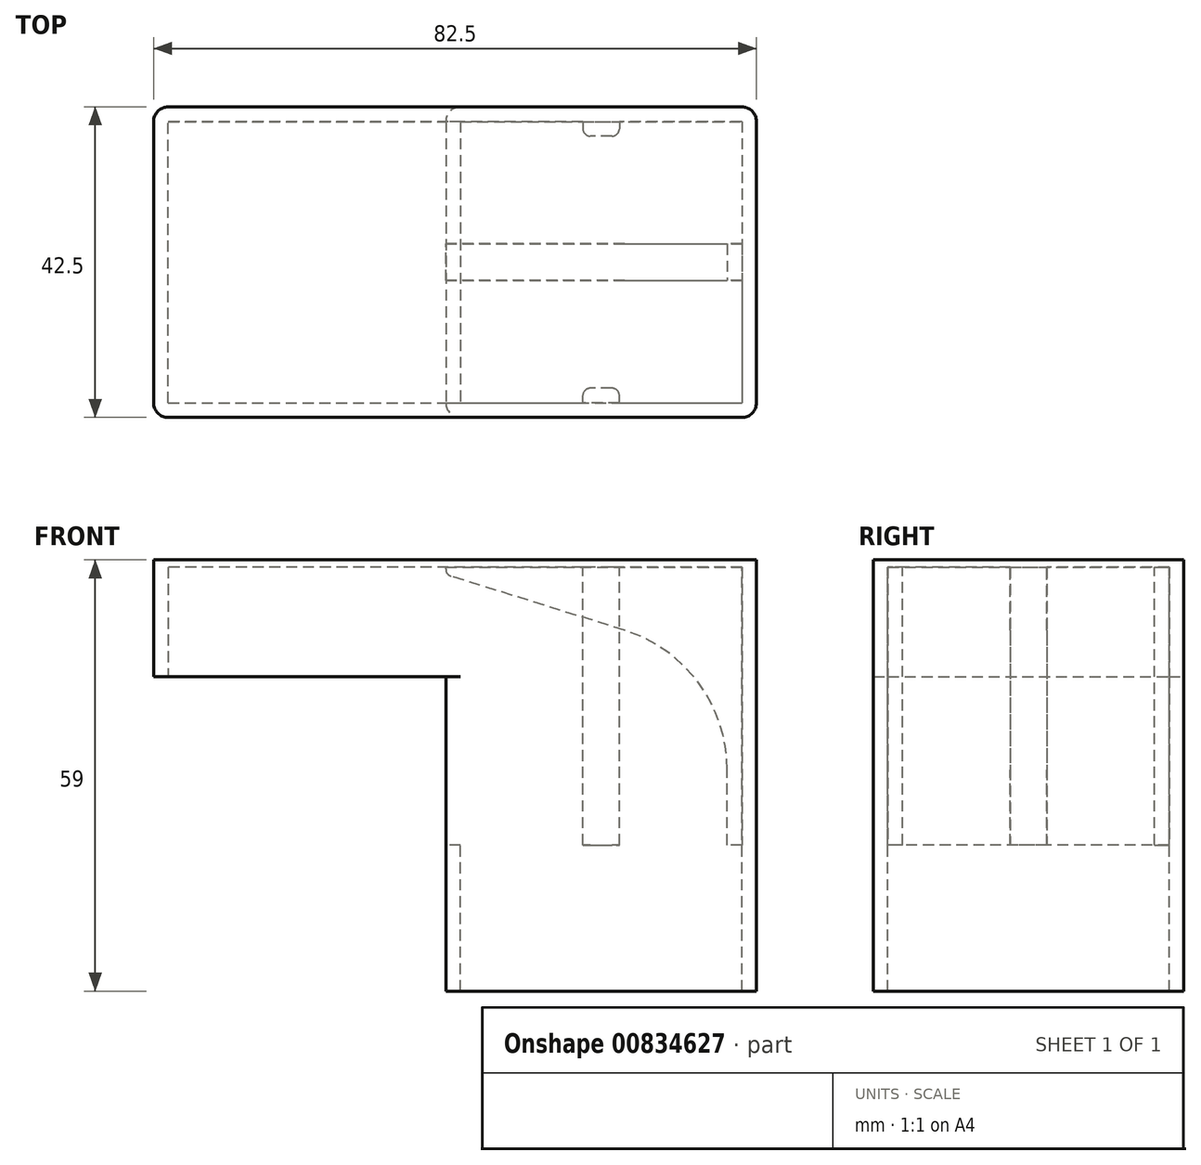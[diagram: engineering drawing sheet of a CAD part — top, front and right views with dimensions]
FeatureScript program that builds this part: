
annotation { "Feature Type Name" : "Feature", "Feature Type Description" : "" }
export const myFeature = defineFeature(function(context is Context, id is Id, definition is map)
    precondition{}
    {
        {
            var Q0;
            Q0=qCreatedBy(makeId("Top.planeOp"),FACE);
            var sketch = newSketch(context, id + "F0", { "sketchPlane" : qUnion([Q0])});
            skLineSegment(sketch, "E0.bottom", {"start": v(-19.25, 19.25) * mm, "end": v(19.25, 19.25) * mm});
            skLineSegment(sketch, "E0.top", {"start": v(-19.25, -19.25) * mm, "end": v(19.25, -19.25) * mm});
            skLineSegment(sketch, "E0.left", {"start": v(-19.25, 19.25) * mm, "end": v(-19.25, -19.25) * mm});
            skLineSegment(sketch, "E0.right", {"start": v(19.25, 19.25) * mm, "end": v(19.25, -19.25) * mm});
            skPoint(sketch, "E0.middle", {"position": v(0, 0) * mm});
            skLineSegment(sketch, "E1.0", {"start": v(-21.25, 21.25) * mm, "end": v(-21.25, -21.25) * mm});
            skLineSegment(sketch, "E1.1", {"start": v(-21.25, 21.25) * mm, "end": v(21.25, 21.25) * mm});
            skLineSegment(sketch, "E1.2", {"start": v(21.25, 21.25) * mm, "end": v(21.25, -21.25) * mm});
            skLineSegment(sketch, "E1.3", {"start": v(-21.25, -21.25) * mm, "end": v(21.25, -21.25) * mm});
            skSolve(sketch);
        }
        {
            var Q0;
            Q0=makeQuery(id+"F0.imprint","IMPRINT",FACE,{"disambiguationData":[TD([[makeQuery(id+"F0.imprint","IMPRINT",EDGE,{"derivedFrom":sQuery(id+"F0.wireOp",EDGE,"E0.bottom")}),1.0]])]});
            extrude(context, id + "F1", {"entities" : qUnion([Q0]), "oppositeDirection" : true, "depth" : 20 * mm, "offsetDistance" : 25 * mm});
        }
        {
            var Q0;
            Q0=makeQuery(id+"F0.imprint","IMPRINT",FACE,{"disambiguationData":[TD([[makeQuery(id+"F0.imprint","IMPRINT",EDGE,{"derivedFrom":sQuery(id+"F0.wireOp",EDGE,"E0.bottom")}),1.0]])]});
            var sketch = newSketch(context, id + "F2", { "sketchPlane" : qUnion([Q0])});
            skLineSegment(sketch, "E2.0", {"start": v(-21.25, -21.25) * mm, "end": v(21.25, -21.25) * mm});
            skLineSegment(sketch, "E3.0", {"start": v(21.25, 21.25) * mm, "end": v(21.25, -21.25) * mm});
            skLineSegment(sketch, "E4.0", {"start": v(19.25, 19.25) * mm, "end": v(19.25, -19.25) * mm});
            skLineSegment(sketch, "E5.0", {"start": v(-21.25, 21.25) * mm, "end": v(21.25, 21.25) * mm});
            skLineSegment(sketch, "E6.0", {"start": v(-21.25, 21.25) * mm, "end": v(-21.25, 19.25) * mm});
            skLineSegment(sketch, "E7", {"start": v(19.25, -19.25) * mm, "end": v(-21.25, -19.25) * mm});
            skLineSegment(sketch, "E8", {"start": v(19.25, 19.25) * mm, "end": v(-21.25, 19.25) * mm});
            skLineSegment(sketch, "E9.trimOffspring", {"start": v(-21.25, -19.25) * mm, "end": v(-21.25, -21.25) * mm});
            skSolve(sketch);
        }
        {
            var Q0;
            Q0=makeQuery(id+"F2.imprint","IMPRINT",FACE,{"disambiguationData":[TD([[makeQuery(id+"F2.imprint","IMPRINT",EDGE,{"derivedFrom":sQuery(id+"F2.wireOp",EDGE,"E2.0")}),1.0]])]});
            extrude(context, id + "F3", {"entities" : qUnion([Q0]), "operationType" : NewBodyOperationType.ADD, "depth" : 38 * mm, "offsetDistance" : 25 * mm});
        }
        {
            var Q0;
            Q0=makeQuery(id+"F3.opExtrude","CAP_FACE",FACE,{"disambiguationData":[OSD([sQuery(id+"F2.wireOp",EDGE,"E2.0"),sQuery(id+"F2.wireOp",EDGE,"E3.0"),sQuery(id+"F2.wireOp",EDGE,"E4.0"),sQuery(id+"F2.wireOp",EDGE,"E5.0"),sQuery(id+"F2.wireOp",EDGE,"E6.0"),sQuery(id+"F2.wireOp",EDGE,"E7"),sQuery(id+"F2.wireOp",EDGE,"E8"),sQuery(id+"F2.wireOp",EDGE,"E9.trimOffspring")])],"isStart":false});
            var sketch = newSketch(context, id + "F4", { "sketchPlane" : qUnion([Q0])});
            skLineSegment(sketch, "E10.bottom", {"start": v(-21.25, -21.25) * mm, "end": v(21.25, -21.25) * mm});
            skLineSegment(sketch, "E10.top", {"start": v(-21.25, 21.25) * mm, "end": v(21.25, 21.25) * mm});
            skLineSegment(sketch, "E10.left", {"start": v(-21.25, -21.25) * mm, "end": v(-21.25, 21.25) * mm});
            skLineSegment(sketch, "E10.right", {"start": v(21.25, -21.25) * mm, "end": v(21.25, 21.25) * mm});
            skSolve(sketch);
        }
        {
            var Q0;
            Q0 = qSketchRegion(id + "F4", true);
            extrude(context, id + "F5", {"entities" : qUnion([Q0]), "operationType" : NewBodyOperationType.ADD, "depth" : 1 * mm, "offsetDistance" : 25 * mm});
        }
        {
            var Q0;
            Q0=makeQuery(id+"F1.opExtrude","CAP_EDGE",EDGE,{"disambiguationData":[OSD([sQuery(id+"F0.wireOp",EDGE,"E0.left")])],"isStart":false});
            cPoint(context, id + "F6", {"entities" : qUnion([Q0]), "parameter" : 0.5});
        }
        {
            var Q0;
            Q0=makeQuery(id+"F3.boolean.opBoolean","MERGE",FACE,{"derivedFrom":[makeQuery(id+"F1.opExtrude","SWEPT_FACE",FACE,{"disambiguationData":[OSD([sQuery(id+"F0.wireOp",EDGE,"E0.top")])]}),makeQuery(id+"F3.opExtrude","SWEPT_FACE",FACE,{"disambiguationData":[OSD([sQuery(id+"F2.wireOp",EDGE,"E7")])]})]});
            var Q1;
            Q1 = qCreatedBy(id + "F6" ,VERTEX);
            cPlane(context, id + "F7", {"entities" : qUnion([Q0, Q1]), "cplaneType" : CPlaneType.PLANE_POINT, "offset" : 25 * mm, "width" : 150 * mm, "height" : 150 * mm});
        }
        {
            var Q0;
            Q0=qCreatedBy(id+"F7.planeOp",FACE);
            var sketch = newSketch(context, id + "F8", { "sketchPlane" : qUnion([Q0])});
            skLineSegment(sketch, "E11.0", {"start": v(21.25, 38) * mm, "end": v(21.25, 37.74) * mm, "construction": true});
            skLineSegment(sketch, "E12.0", {"start": v(21.25, 38) * mm, "end": v(-19.25, 38) * mm});
            skLineSegment(sketch, "E13", {"start": v(-19.25, 38) * mm, "end": v(-19.25, 0) * mm});
            skLineSegment(sketch, "E14", {"start": v(-19.25, 0) * mm, "end": v(-17.25, 0) * mm});
            skLineSegment(sketch, "E15", {"start": v(-17.25, 0) * mm, "end": v(-17.25, 10.28) * mm});
            skLineSegment(sketch, "E16", {"start": v(-3.2, 29.38) * mm, "end": v(20.55, 36.78) * mm});
            skLineSegment(sketch, "E17", {"start": v(21.25, 37) * mm, "end": v(21.25, 38) * mm});
            skPoint(sketch, "E18.visualSharp", {"position": v(-17.25, 0) * mm});
            skLineSegment(sketch, "E18.filletArc", {"start": v(-17.25, 0) * mm, "end": v(-17.25, 0) * mm});
            skPoint(sketch, "E19.visualSharp", {"position": v(-17.25, 25) * mm});
            skArc(sketch, "E19.filletArc", {"start": v(-3.2, 29.38) * mm, "mid": v(-13.36, 22.14) * mm, "end": v(-17.25, 10.28) * mm});
            skPoint(sketch, "E20.orphan", {"position": v(21.25, 0) * mm});
            skPoint(sketch, "E21.visualSharp", {"position": v(21.25, 37) * mm});
            skArc(sketch, "E21.filletArc", {"start": v(20.55, 36.78) * mm, "mid": v(21.06, 37.14) * mm, "end": v(21.25, 37.74) * mm});
            skSolve(sketch);
        }
        {
            var Q0;
            {var subQ0=sQuery(id+"F8.wireOp",EDGE,"E12.0");Q0=makeQuery(id+"F8.imprint","IMPRINT",FACE,{"disambiguationData":[TD([[makeQuery(id+"F8.imprint","IMPRINT",EDGE,{"derivedFrom":subQ0}),1.0]])]});}
            extrude(context, id + "F9", {"entities" : qUnion([Q0]), "operationType" : NewBodyOperationType.ADD, "endBound" : BoundingType.SYMMETRIC, "depth" : 5 * mm, "offsetDistance" : 25 * mm});
        }
        {
            var Q0;
            Q0=makeQuery(id+"F9.boolean.opBoolean","MERGE",FACE,{"derivedFrom":[makeQuery(id+"F5.boolean.opBoolean","MERGE",FACE,{"derivedFrom":[makeQuery(id+"F3.boolean.opBoolean","MERGE",FACE,{"derivedFrom":[makeQuery(id+"F1.opExtrude","SWEPT_FACE",FACE,{"disambiguationData":[OSD([sQuery(id+"F0.wireOp",EDGE,"E1.0")])]}),makeQuery(id+"F3.opExtrude","SWEPT_FACE",FACE,{"disambiguationData":[OSD([sQuery(id+"F2.wireOp",EDGE,"E6.0")])]}),makeQuery(id+"F3.opExtrude","SWEPT_FACE",FACE,{"disambiguationData":[OSD([sQuery(id+"F2.wireOp",EDGE,"E9.trimOffspring")])]})]}),makeQuery(id+"F5.opExtrude","SWEPT_FACE",FACE,{"disambiguationData":[OSD([sQuery(id+"F4.wireOp",EDGE,"E10.left")])]})]}),makeQuery(id+"F9.opExtrude","SWEPT_FACE",FACE,{"disambiguationData":[OSD([sQuery(id+"F8.wireOp",EDGE,"E17")])]})]});
            var sketch = newSketch(context, id + "F10", { "sketchPlane" : qUnion([Q0])});
            skLineSegment(sketch, "E22.0", {"start": v(19.25, 38) * mm, "end": v(19.25, 23) * mm});
            skLineSegment(sketch, "E23.0", {"start": v(-19.25, 38) * mm, "end": v(-19.25, 23) * mm});
            skLineSegment(sketch, "E24.0", {"start": v(-21.25, 39) * mm, "end": v(21.25, 39) * mm});
            skLineSegment(sketch, "E25", {"start": v(19.25, 38) * mm, "end": v(-19.25, 38) * mm});
            skLineSegment(sketch, "E26", {"start": v(21.25, 39) * mm, "end": v(21.25, 23) * mm});
            skLineSegment(sketch, "E27", {"start": v(-21.25, 39) * mm, "end": v(-21.25, 23) * mm});
            skLineSegment(sketch, "E28", {"start": v(21.25, 23) * mm, "end": v(-21.25, 23) * mm});
            skPoint(sketch, "E29.end.orphan", {"position": v(19.25, 0) * mm});
            skPoint(sketch, "E29.start.orphan", {"position": v(21.25, 0) * mm});
            skPoint(sketch, "E30.trimOffspring.start.orphan", {"position": v(-19.25, 0) * mm});
            skSolve(sketch);
        }
        {
            var Q0;
            {var subQ4=sQuery(id+"F10.wireOp",EDGE,"E22.0");Q0=makeQuery(id+"F10.imprint","IMPRINT",FACE,{"disambiguationData":[TD([[makeQuery(id+"F10.imprint","IMPRINT",EDGE,{"derivedFrom":subQ4}),1.0]])]});}
            extrude(context, id + "F11", {"entities" : qUnion([Q0]), "operationType" : NewBodyOperationType.ADD, "depth" : 38 * mm, "offsetDistance" : 25 * mm});
        }
        {
            var Q0;
            Q0=makeQuery(id+"F11.opExtrude","CAP_FACE",FACE,{"disambiguationData":[OSD([sQuery(id+"F10.wireOp",EDGE,"E22.0"),sQuery(id+"F10.wireOp",EDGE,"E23.0"),sQuery(id+"F10.wireOp",EDGE,"E24.0"),sQuery(id+"F10.wireOp",EDGE,"E25"),sQuery(id+"F10.wireOp",EDGE,"E26"),sQuery(id+"F10.wireOp",EDGE,"E27"),sQuery(id+"F10.wireOp",EDGE,"E28")])],"isStart":false});
            var sketch = newSketch(context, id + "F12", { "sketchPlane" : qUnion([Q0])});
            skLineSegment(sketch, "E31.bottom", {"start": v(21.25, 39) * mm, "end": v(-21.25, 39) * mm});
            skLineSegment(sketch, "E31.top", {"start": v(21.25, 23) * mm, "end": v(-21.25, 23) * mm});
            skLineSegment(sketch, "E31.left", {"start": v(21.25, 39) * mm, "end": v(21.25, 23) * mm});
            skLineSegment(sketch, "E31.right", {"start": v(-21.25, 39) * mm, "end": v(-21.25, 23) * mm});
            skSolve(sketch);
        }
        {
            var Q0;
            Q0 = qSketchRegion(id + "F12", true);
            extrude(context, id + "F13", {"entities" : qUnion([Q0]), "operationType" : NewBodyOperationType.ADD, "depth" : 2 * mm, "offsetDistance" : 25 * mm});
        }
        {
            var Q0;
            {var subQ5=sQuery(id+"F4.wireOp",EDGE,"E10.left");var subQ16=makeQuery(id+"F5.opExtrude","CAP_FACE",FACE,{"disambiguationData":[OSD([sQuery(id+"F4.wireOp",EDGE,"E10.bottom"),sQuery(id+"F4.wireOp",EDGE,"E10.top"),subQ5,sQuery(id+"F4.wireOp",EDGE,"E10.right")])],"isStart":true});Q0=makeQuery(id+"F11.boolean.opBoolean","MERGE",FACE,{"derivedFrom":[makeQuery(id+"F9.boolean.opBoolean","SPLIT",FACE,{"disambiguationData":[TD([makeQuery(id+"F1.opExtrude","SWEPT_FACE",FACE,{"disambiguationData":[OSD([sQuery(id+"F0.wireOp",EDGE,"E0.top")])]})])],"derivedFrom":subQ16}),makeQuery(id+"F9.boolean.opBoolean","SPLIT",FACE,{"disambiguationData":[TD([makeQuery(id+"F1.opExtrude","SWEPT_FACE",FACE,{"disambiguationData":[OSD([sQuery(id+"F0.wireOp",EDGE,"E0.bottom")])]})])],"derivedFrom":subQ16}),makeQuery(id+"F11.opExtrude","SWEPT_FACE",FACE,{"disambiguationData":[OSD([sQuery(id+"F10.wireOp",EDGE,"E25")])]})]});}
            var sketch = newSketch(context, id + "F14", { "sketchPlane" : qUnion([Q0])});
            skLineSegment(sketch, "E32.0", {"start": v(-19.25, 19.25) * mm, "end": v(19.25, 19.25) * mm, "construction": true});
            skLineSegment(sketch, "E33.bottom", {"start": v(2.5, 19.25) * mm, "end": v(-2.5, 19.25) * mm});
            skLineSegment(sketch, "E33.top", {"start": v(1.5, 17.25) * mm, "end": v(-1.5, 17.25) * mm});
            skLineSegment(sketch, "E33.left", {"start": v(2.5, 19.25) * mm, "end": v(2.5, 18.25) * mm});
            skLineSegment(sketch, "E33.right", {"start": v(-2.5, 19.25) * mm, "end": v(-2.5, 18.25) * mm});
            skPoint(sketch, "E33.middle", {"position": v(0, 18.25) * mm});
            skPoint(sketch, "E33.middle.positionSnap0", {"position": v(0, 19.25) * mm});
            skPoint(sketch, "E33.centerSnap0", {"position": v(0, 19.25) * mm});
            skLineSegment(sketch, "E34.MirrorCS", {"start": v(1.5, -17.25) * mm, "end": v(-1.5, -17.25) * mm});
            skLineSegment(sketch, "E35.MirrorCS", {"start": v(2.5, -19.25) * mm, "end": v(2.5, -18.25) * mm});
            skLineSegment(sketch, "E36.MirrorCS", {"start": v(-2.5, -19.25) * mm, "end": v(-2.5, -18.25) * mm});
            skLineSegment(sketch, "E37", {"start": v(2.5, -19.25) * mm, "end": v(-2.5, -19.25) * mm});
            skPoint(sketch, "E38.visualSharp", {"position": v(2.5, 17.25) * mm});
            skArc(sketch, "E38.filletArc", {"start": v(1.5, 17.25) * mm, "mid": v(2.2, 17.54) * mm, "end": v(2.5, 18.25) * mm});
            skPoint(sketch, "E39.visualSharp", {"position": v(-2.5, 17.25) * mm});
            skArc(sketch, "E39.filletArc", {"start": v(-2.5, 18.25) * mm, "mid": v(-2.2, 17.54) * mm, "end": v(-1.5, 17.25) * mm});
            skPoint(sketch, "E40.visualSharp", {"position": v(2.5, -17.25) * mm});
            skArc(sketch, "E40.filletArc", {"start": v(2.5, -18.25) * mm, "mid": v(2.2, -17.54) * mm, "end": v(1.5, -17.25) * mm});
            skPoint(sketch, "E41.visualSharp", {"position": v(-2.5, -17.25) * mm});
            skArc(sketch, "E41.filletArc", {"start": v(-1.5, -17.25) * mm, "mid": v(-2.2, -17.54) * mm, "end": v(-2.5, -18.25) * mm});
            skSolve(sketch);
        }
        {
            var Q0;
            Q0=makeQuery(id+"F14.imprint","IMPRINT",FACE,{"disambiguationData":[TD([[makeQuery(id+"F14.imprint","IMPRINT",EDGE,{"derivedFrom":sQuery(id+"F14.wireOp",EDGE,"E33.bottom")}),-1.0]])]});
            var Q1;
            Q1=makeQuery(id+"F14.imprint","IMPRINT",FACE,{"disambiguationData":[TD([[makeQuery(id+"F14.imprint","IMPRINT",EDGE,{"derivedFrom":sQuery(id+"F14.wireOp",EDGE,"E34.MirrorCS")}),1.0]])]});
            var Q2;
            Q2=makeQuery(id+"F9.opExtrude","SWEPT_FACE",FACE,{"disambiguationData":[OSD([sQuery(id+"F8.wireOp",EDGE,"E14")])]});
            extrude(context, id + "F15", {"entities" : qUnion([Q0, Q1]), "operationType" : NewBodyOperationType.ADD, "endBound" : BoundingType.UP_TO_SURFACE, "depth" : 25 * mm, "endBoundEntityFace" : qUnion([Q2]), "offsetDistance" : 25 * mm});
        }
        {
            var Q0;
            Q0=makeQuery(id+"F5.boolean.opBoolean","MERGE",EDGE,{"derivedFrom":[makeQuery(id+"F3.boolean.opBoolean","MERGE",EDGE,{"derivedFrom":[makeQuery(id+"F1.opExtrude","SWEPT_EDGE",EDGE,{"disambiguationData":[OSD([sQuery(id+"F0.wireOp",EDGE,"E1.1"),sQuery(id+"F0.wireOp",EDGE,"E1.2")])]}),makeQuery(id+"F3.opExtrude","SWEPT_EDGE",EDGE,{"disambiguationData":[OSD([sQuery(id+"F2.wireOp",EDGE,"E3.0"),sQuery(id+"F2.wireOp",EDGE,"E5.0")])]})]}),makeQuery(id+"F5.opExtrude","SWEPT_EDGE",EDGE,{"disambiguationData":[OSD([sQuery(id+"F4.wireOp",EDGE,"E10.top"),sQuery(id+"F4.wireOp",EDGE,"E10.right")])]})]});
            var Q1;
            Q1=makeQuery(id+"F5.boolean.opBoolean","MERGE",EDGE,{"derivedFrom":[makeQuery(id+"F3.boolean.opBoolean","MERGE",EDGE,{"derivedFrom":[makeQuery(id+"F1.opExtrude","SWEPT_EDGE",EDGE,{"disambiguationData":[OSD([sQuery(id+"F0.wireOp",EDGE,"E1.0"),sQuery(id+"F0.wireOp",EDGE,"E1.1")])]}),makeQuery(id+"F3.opExtrude","SWEPT_EDGE",EDGE,{"disambiguationData":[OSD([sQuery(id+"F2.wireOp",EDGE,"E5.0"),sQuery(id+"F2.wireOp",EDGE,"E6.0")])]})]}),makeQuery(id+"F5.opExtrude","SWEPT_EDGE",EDGE,{"disambiguationData":[OSD([sQuery(id+"F4.wireOp",EDGE,"E10.top"),sQuery(id+"F4.wireOp",EDGE,"E10.left")])]})]});
            var Q2;
            Q2=makeQuery(id+"F13.opExtrude","CAP_EDGE",EDGE,{"disambiguationData":[OSD([sQuery(id+"F12.wireOp",EDGE,"E31.right")])],"isStart":false});
            var Q3;
            Q3=makeQuery(id+"F13.opExtrude","CAP_EDGE",EDGE,{"disambiguationData":[OSD([sQuery(id+"F12.wireOp",EDGE,"E31.left")])],"isStart":false});
            var Q4;
            Q4=makeQuery(id+"F5.boolean.opBoolean","MERGE",EDGE,{"derivedFrom":[makeQuery(id+"F3.boolean.opBoolean","MERGE",EDGE,{"derivedFrom":[makeQuery(id+"F1.opExtrude","SWEPT_EDGE",EDGE,{"disambiguationData":[OSD([sQuery(id+"F0.wireOp",EDGE,"E1.0"),sQuery(id+"F0.wireOp",EDGE,"E1.3")])]}),makeQuery(id+"F3.opExtrude","SWEPT_EDGE",EDGE,{"disambiguationData":[OSD([sQuery(id+"F2.wireOp",EDGE,"E2.0"),sQuery(id+"F2.wireOp",EDGE,"E9.trimOffspring")])]})]}),makeQuery(id+"F5.opExtrude","SWEPT_EDGE",EDGE,{"disambiguationData":[OSD([sQuery(id+"F4.wireOp",EDGE,"E10.bottom"),sQuery(id+"F4.wireOp",EDGE,"E10.left")])]})]});
            var Q5;
            Q5=makeQuery(id+"F5.boolean.opBoolean","MERGE",EDGE,{"derivedFrom":[makeQuery(id+"F3.boolean.opBoolean","MERGE",EDGE,{"derivedFrom":[makeQuery(id+"F1.opExtrude","SWEPT_EDGE",EDGE,{"disambiguationData":[OSD([sQuery(id+"F0.wireOp",EDGE,"E1.2"),sQuery(id+"F0.wireOp",EDGE,"E1.3")])]}),makeQuery(id+"F3.opExtrude","SWEPT_EDGE",EDGE,{"disambiguationData":[OSD([sQuery(id+"F2.wireOp",EDGE,"E2.0"),sQuery(id+"F2.wireOp",EDGE,"E3.0")])]})]}),makeQuery(id+"F5.opExtrude","SWEPT_EDGE",EDGE,{"disambiguationData":[OSD([sQuery(id+"F4.wireOp",EDGE,"E10.bottom"),sQuery(id+"F4.wireOp",EDGE,"E10.right")])]})]});
            fillet(context, id + "F16", {"entities" : qUnion([Q0, Q1, Q2, Q3, Q4, Q5]), "radius" : 2 * mm, "allowEdgeOverflow" : false});
        }
    });
